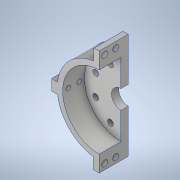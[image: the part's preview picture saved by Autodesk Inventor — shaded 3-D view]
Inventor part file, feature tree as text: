
AUTODESK INVENTOR PART (.ipt)
format: ipt  version: 2020 (Build 240168000, 168)  size: 249,344 bytes
history: native  units: mm
features: extrude x7, sketch x7, projected_geometry x6, other x1
ambient origin geometry x8: Origin, YZ Plane, XZ Plane, XY Plane, X Axis, Y Axis, Z Axis, Center Point
bodies: Body1 (feature_tree)
feature tree (21):
  other  "솔리드1"
  extrude  "돌출1"  Depth=10.4mm
  extrude  "돌출2"  Depth=46.0mm
  extrude  "돌출3"  Depth=4.0mm TaperAngle=0.0deg
  extrude  "돌출4"  Depth=40.0mm
  extrude  "돌출5"  Depth=46.0mm
  extrude  "돌출6"  Depth=29.0mm
  extrude  "돌출7"  Depth=29.0mm
  sketch  "스케치1"
  sketch  "스케치2"
  sketch  "스케치3"
  projected_geometry  "투영된 루프1"
  projected_geometry  "투영된 루프2"
  sketch  "스케치4"
  sketch  "스케치5"
  sketch  "스케치6"
  projected_geometry  "투영된 루프3"
  sketch  "스케치7"
  projected_geometry  "투영된 루프4"
  projected_geometry  "투영된 루프5"
  projected_geometry  "투영된 루프6"
